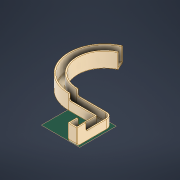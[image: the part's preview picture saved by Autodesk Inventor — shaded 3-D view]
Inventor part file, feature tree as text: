
AUTODESK INVENTOR PART (.ipt)
format: ipt  version: 2021 (Build 250183000, 183)  size: 260,608 bytes
history: native  units: mm
features: sketch x4, sweep x2, fillet x2, plane x1
ambient origin geometry x8: Origin, YZ Plane, XZ Plane, XY Plane, X Axis, Y Axis, Z Axis, Center Point
bodies: Solid1 (feature_tree)
feature tree (9):
  sweep  "Sweep1"
  sketch  "Sketch2"  dims[d2=4.0mm d3=30.0mm d4=30.0mm d5=0.0mm]
  plane  "Work Plane1"
  sweep  "Sweep2"
  fillet  "Fillet1"  Radius=30.0mm
  fillet  "Fillet2"  [1 undecoded]
  sketch  "Sketch1"  dims[d0=4.0mm d1=4.0mm]
  sketch  "3D Sketch1"
  sketch  "Sketch3"  dims[d6=15.0mm d7=5.0mm d8=5.0mm d9=50.0mm d10=100.0mm d11=100.0mm d12=0.0mm d13=0.0mm d14=4.0mm d15=0.0mm d16=50.0mm d17=50.0mm d18=0.0mm d19=30.0mm d20=0.0mm d21=0.0mm d22=5.0mm d23=2.0mm]
note: 1 required parameter value undecoded (feature->parameter linkage not recoverable at this tier; creation-order binding heuristic only, values carry confidence <= 0.55)
